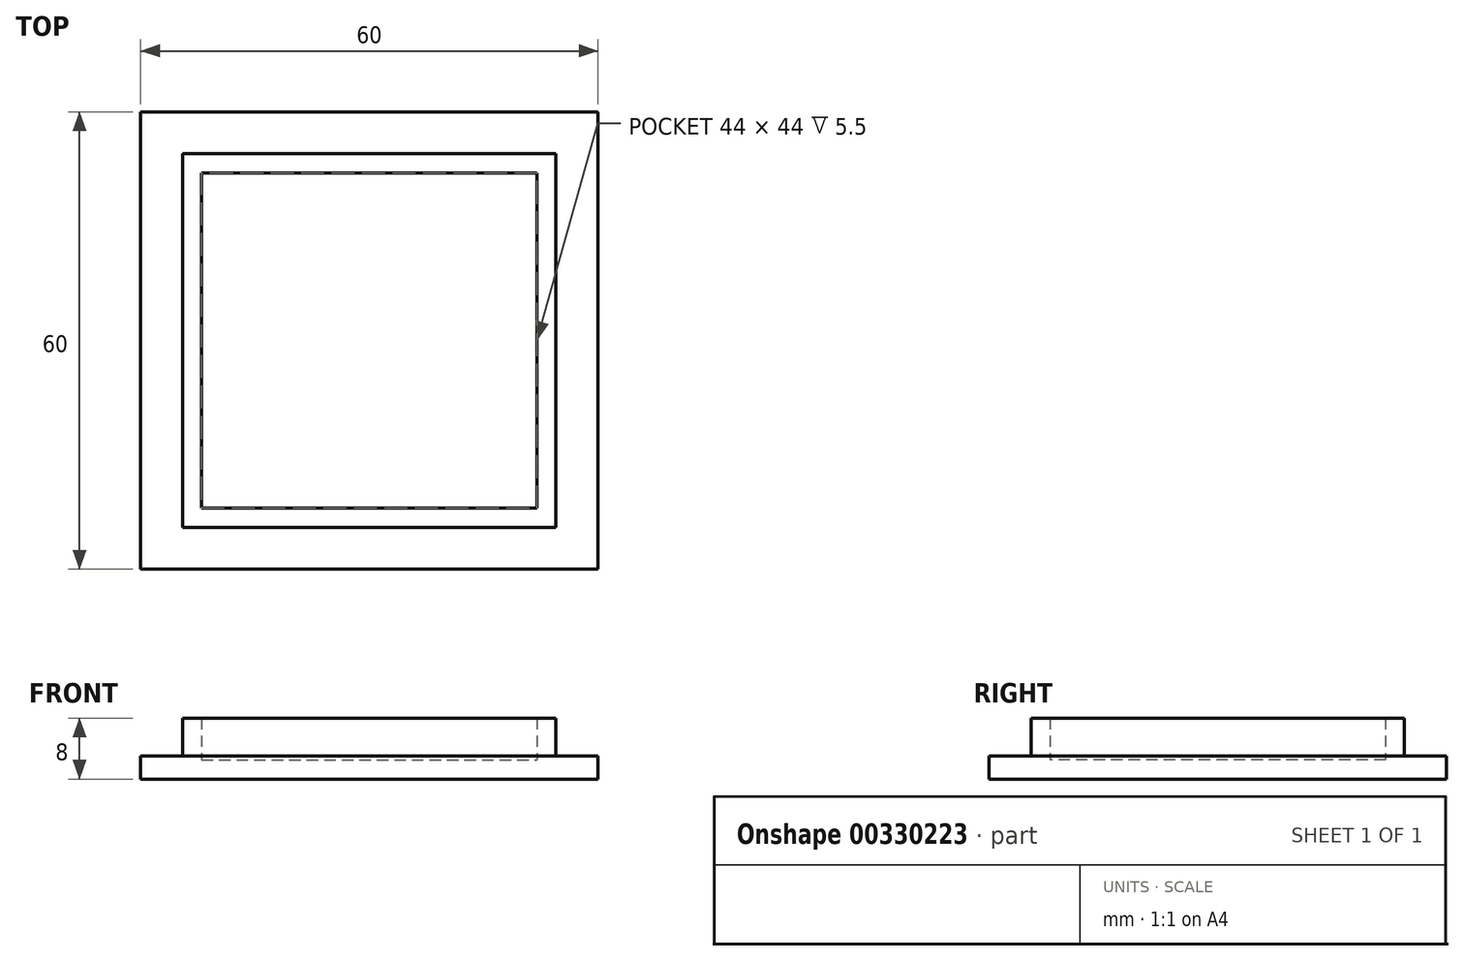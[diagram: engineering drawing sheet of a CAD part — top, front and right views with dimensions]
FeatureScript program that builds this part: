
annotation { "Feature Type Name" : "Feature", "Feature Type Description" : "" }
export const myFeature = defineFeature(function(context is Context, id is Id, definition is map)
    precondition{}
    {
        {
            var Q0;
            Q0=qCreatedBy(makeId("Top.planeOp"),FACE);
            var sketch = newSketch(context, id + "F0", { "sketchPlane" : qUnion([Q0])});
            skLineSegment(sketch, "E0.bottom", {"start": v(30, -30) * mm, "end": v(-30, -30) * mm});
            skLineSegment(sketch, "E0.top", {"start": v(30, 30) * mm, "end": v(-30, 30) * mm});
            skLineSegment(sketch, "E0.left", {"start": v(30, -30) * mm, "end": v(30, 30) * mm});
            skLineSegment(sketch, "E0.right", {"start": v(-30, -30) * mm, "end": v(-30, 30) * mm});
            skPoint(sketch, "E0.middle", {"position": v(0, 0) * mm});
            skSolve(sketch);
        }
        {
            var Q0;
            Q0 = qSketchRegion(id + "F0", true);
            extrude(context, id + "F1", {"entities" : qUnion([Q0]), "depth" : 3 * mm});
        }
        {
            var Q0;
            Q0=makeQuery(id+"F1.opExtrude","CAP_FACE",FACE,{"disambiguationData":[OSD([sQuery(id+"F0.wireOp",EDGE,"E0.bottom"),sQuery(id+"F0.wireOp",EDGE,"E0.top"),sQuery(id+"F0.wireOp",EDGE,"E0.left"),sQuery(id+"F0.wireOp",EDGE,"E0.right")])],"isStart":false});
            var sketch = newSketch(context, id + "F2", { "sketchPlane" : qUnion([Q0])});
            skLineSegment(sketch, "E1.bottom", {"start": v(24.5, -24.5) * mm, "end": v(-24.5, -24.5) * mm});
            skLineSegment(sketch, "E1.top", {"start": v(24.5, 24.5) * mm, "end": v(-24.5, 24.5) * mm});
            skLineSegment(sketch, "E1.left", {"start": v(24.5, -24.5) * mm, "end": v(24.5, 24.5) * mm});
            skLineSegment(sketch, "E1.right", {"start": v(-24.5, -24.5) * mm, "end": v(-24.5, 24.5) * mm});
            skPoint(sketch, "E1.middle", {"position": v(0, 0) * mm});
            skSolve(sketch);
        }
        {
            var Q0;
            Q0 = qSketchRegion(id + "F2", true);
            extrude(context, id + "F3", {"entities" : qUnion([Q0]), "operationType" : NewBodyOperationType.ADD, "depth" : 5 * mm});
        }
        {
            var Q0;
            Q0=makeQuery(id+"F3.opExtrude","CAP_FACE",FACE,{"disambiguationData":[OSD([sQuery(id+"F2.wireOp",EDGE,"E1.bottom"),sQuery(id+"F2.wireOp",EDGE,"E1.top"),sQuery(id+"F2.wireOp",EDGE,"E1.left"),sQuery(id+"F2.wireOp",EDGE,"E1.right")])],"isStart":false});
            shell(context, id + "F4", {"entities" : qUnion([Q0]), "thickness" : 2.5 * mm});
        }
    });
